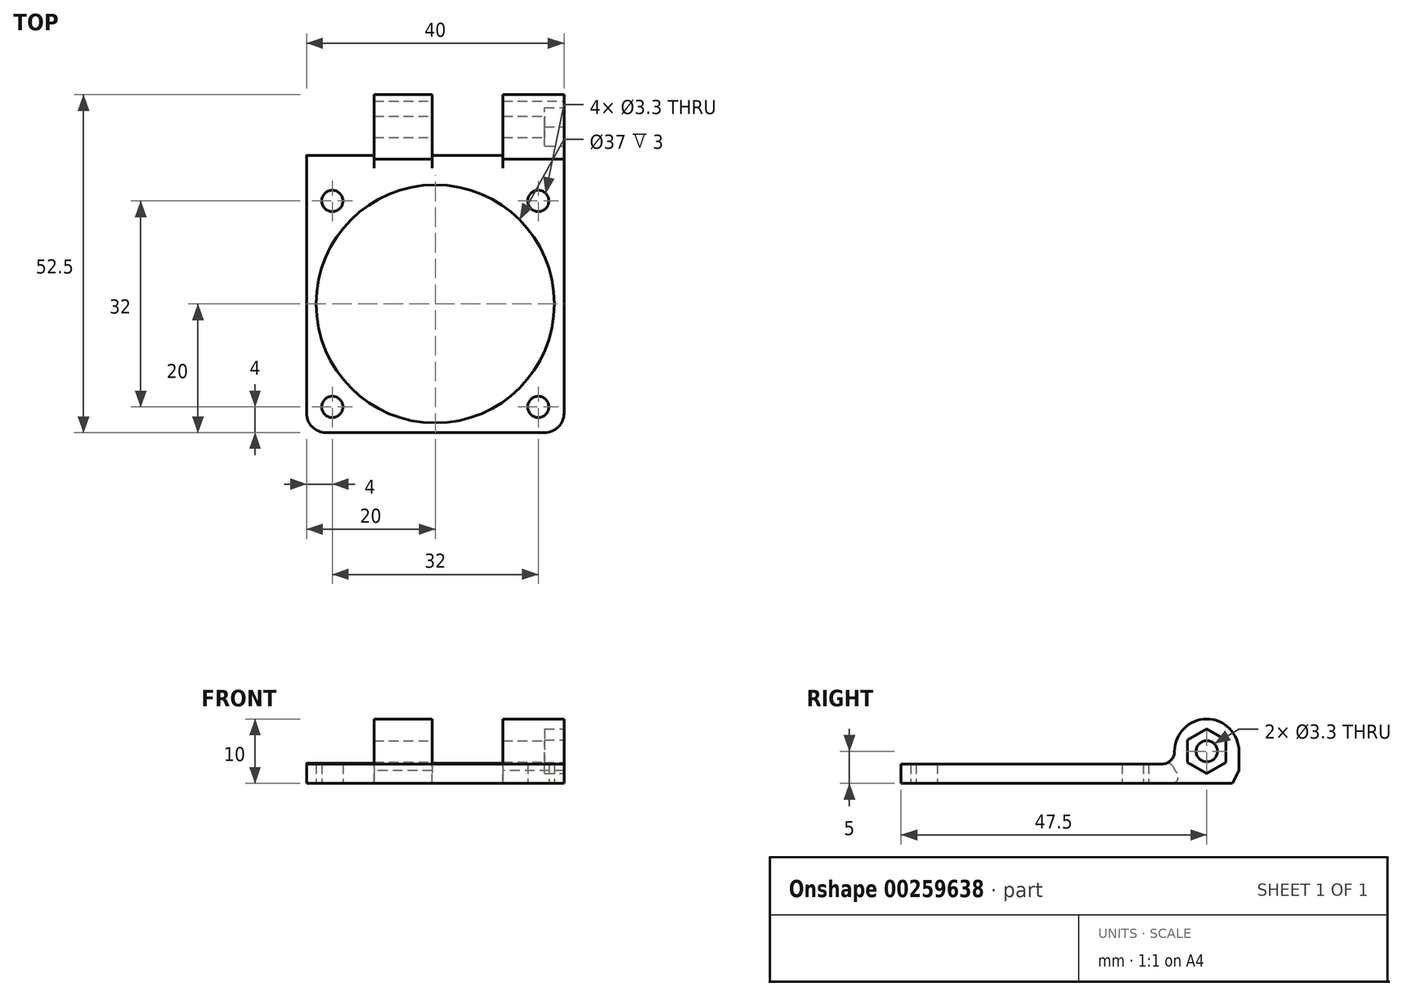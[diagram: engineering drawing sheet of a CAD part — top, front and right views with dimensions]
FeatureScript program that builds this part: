
annotation { "Feature Type Name" : "Feature", "Feature Type Description" : "" }
export const myFeature = defineFeature(function(context is Context, id is Id, definition is map)
    precondition{}
    {
        {
            var Q0;
            Q0=qCreatedBy(makeId("Top.planeOp"),FACE);
            var sketch = newSketch(context, id + "F0", { "sketchPlane" : qUnion([Q0])});
            skLineSegment(sketch, "E0.bottom", {"start": v(0, 0) * mm, "end": v(40, 0) * mm});
            skLineSegment(sketch, "E0.top", {"start": v(3, -45) * mm, "end": v(37, -45) * mm});
            skLineSegment(sketch, "E0.left", {"start": v(0, 0) * mm, "end": v(0, -42) * mm});
            skLineSegment(sketch, "E0.right", {"start": v(40, 0) * mm, "end": v(40, -42) * mm});
            skLineSegment(sketch, "E1", {"start": v(0, -5) * mm, "end": v(40, -5) * mm, "construction": true});
            skLineSegment(sketch, "E2", {"start": v(20, -5) * mm, "end": v(20, -45) * mm, "construction": true});
            skLineSegment(sketch, "E3", {"start": v(0, -5) * mm, "end": v(40, -45) * mm, "construction": true});
            skLineSegment(sketch, "E4", {"start": v(0, -45) * mm, "end": v(40, -5) * mm, "construction": true});
            skCircle(sketch, "E5", {"center": v(20, -25) * mm, "radius": 18.5 * mm});
            skCircle(sketch, "E6", {"center": v(4, -9) * mm, "radius": 1.65 * mm});
            skCircle(sketch, "E7", {"center": v(36, -9) * mm, "radius": 1.65 * mm});
            skCircle(sketch, "E8", {"center": v(36, -41) * mm, "radius": 1.65 * mm});
            skCircle(sketch, "E9", {"center": v(4, -41) * mm, "radius": 1.65 * mm});
            skPoint(sketch, "E10.visualSharp", {"position": v(0, -45) * mm});
            skArc(sketch, "E10.filletArc", {"start": v(0, -42) * mm, "mid": v(0.88, -44.12) * mm, "end": v(3, -45) * mm});
            skPoint(sketch, "E11.visualSharp", {"position": v(40, -45) * mm});
            skArc(sketch, "E11.filletArc", {"start": v(37, -45) * mm, "mid": v(39.12, -44.12) * mm, "end": v(40, -42) * mm});
            skSolve(sketch);
        }
        {
            var Q0;
            Q0 = qSketchRegion(id + "F0", true);
            extrude(context, id + "F1", {"entities" : qUnion([Q0]), "depth" : 3 * mm});
        }
        {
            var Q0;
            Q0=qCreatedBy(makeId("Right.planeOp"),FACE);
            var sketch = newSketch(context, id + "F2", { "sketchPlane" : qUnion([Q0])});
            skLineSegment(sketch, "E12.bottom", {"start": v(-2.5, 0) * mm, "end": v(7.5, 0) * mm});
            skLineSegment(sketch, "E12.left", {"start": v(-2.5, 0) * mm, "end": v(-2.5, 5) * mm});
            skArc(sketch, "E13", {"start": v(7.5, 5) * mm, "mid": v(2.5, 10) * mm, "end": v(-2.5, 5) * mm});
            skLineSegment(sketch, "E14", {"start": v(7.5, 5) * mm, "end": v(7.5, 0) * mm});
            skLineSegment(sketch, "E15", {"start": v(-2.5, 5) * mm, "end": v(7.5, 5) * mm, "construction": true});
            skLineSegment(sketch, "E16", {"start": v(2.5, 5) * mm, "end": v(2.5, 0) * mm, "construction": true});
            skSolve(sketch);
        }
        {
            var Q0;
            Q0 = qSketchRegion(id + "F2", true);
            extrude(context, id + "F3", {"entities" : qUnion([Q0]), "operationType" : NewBodyOperationType.ADD, "depth" : 40 * mm});
        }
        {
            var Q0;
            Q0=makeQuery(id+"F3.boolean.opBoolean","MERGE",FACE,{"derivedFrom":[makeQuery(id+"F1.opExtrude","SWEPT_FACE",FACE,{"disambiguationData":[OSD([sQuery(id+"F0.wireOp",EDGE,"E0.right")])]}),makeQuery(id+"F3.opExtrude","CAP_FACE",FACE,{"disambiguationData":[OSD([sQuery(id+"F2.wireOp",EDGE,"E12.bottom"),sQuery(id+"F2.wireOp",EDGE,"E12.left"),sQuery(id+"F2.wireOp",EDGE,"E13")])],"isStart":false})]});
            var sketch = newSketch(context, id + "F4", { "sketchPlane" : qUnion([Q0])});
            skLineSegment(sketch, "E17", {"start": v(0, 0) * mm, "end": v(2.5, 0) * mm, "construction": true});
            skLineSegment(sketch, "E18", {"start": v(2.5, 0) * mm, "end": v(2.5, 5) * mm, "construction": true});
            skCircle(sketch, "E19", {"center": v(2.5, 5) * mm, "radius": 1.65 * mm});
            skSolve(sketch);
        }
        {
            var Q0;
            Q0 = qSketchRegion(id + "F4", true);
            extrude(context, id + "F5", {"entities" : qUnion([Q0]), "operationType" : NewBodyOperationType.REMOVE, "endBound" : BoundingType.THROUGH_ALL, "oppositeDirection" : true, "depth" : 25 * mm});
        }
        {
            var Q0;
            Q0=makeQuery(id+"F3.boolean.opBoolean","MERGE",FACE,{"derivedFrom":[makeQuery(id+"F1.opExtrude","SWEPT_FACE",FACE,{"disambiguationData":[OSD([sQuery(id+"F0.wireOp",EDGE,"E0.right")])]}),makeQuery(id+"F3.opExtrude","CAP_FACE",FACE,{"disambiguationData":[OSD([sQuery(id+"F2.wireOp",EDGE,"E12.bottom"),sQuery(id+"F2.wireOp",EDGE,"E12.left"),sQuery(id+"F2.wireOp",EDGE,"E13")])],"isStart":false})]});
            var sketch = newSketch(context, id + "F6", { "sketchPlane" : qUnion([Q0])});
            skLineSegment(sketch, "E20", {"start": v(0, 0) * mm, "end": v(2.5, 0) * mm, "construction": true});
            skLineSegment(sketch, "E21", {"start": v(2.5, 0) * mm, "end": v(2.5, 5) * mm, "construction": true});
            skCircle(sketch, "E22.cCircle", {"center": v(2.5, 5) * mm, "radius": 3 * mm, "construction": true});
            skLineSegment(sketch, "E22.0", {"start": v(5.5, 6.73) * mm, "end": v(5.5, 3.27) * mm});
            skLineSegment(sketch, "E22.1", {"start": v(5.5, 3.27) * mm, "end": v(2.5, 1.54) * mm});
            skLineSegment(sketch, "E22.2", {"start": v(2.5, 1.54) * mm, "end": v(-0.5, 3.27) * mm});
            skLineSegment(sketch, "E22.3", {"start": v(-0.5, 3.27) * mm, "end": v(-0.5, 6.73) * mm});
            skLineSegment(sketch, "E22.4", {"start": v(-0.5, 6.73) * mm, "end": v(2.5, 8.46) * mm});
            skLineSegment(sketch, "E22.5", {"start": v(2.5, 8.46) * mm, "end": v(5.5, 6.73) * mm});
            skPoint(sketch, "E22.0.midPoint", {"position": v(5.5, 5) * mm});
            skSolve(sketch);
        }
        {
            var Q0;
            Q0 = qSketchRegion(id + "F6", true);
            extrude(context, id + "F7", {"entities" : qUnion([Q0]), "operationType" : NewBodyOperationType.REMOVE, "oppositeDirection" : true, "depth" : 3 * mm});
        }
        {
            var Q0;
            Q0=makeQuery(id+"F3.boolean.opBoolean","INTERSECT",EDGE,{"derivedFrom":[makeQuery(id+"F1.opExtrude","CAP_FACE",FACE,{"disambiguationData":[OSD([sQuery(id+"F0.wireOp",EDGE,"E0.bottom"),sQuery(id+"F0.wireOp",EDGE,"E0.top"),sQuery(id+"F0.wireOp",EDGE,"E0.left"),sQuery(id+"F0.wireOp",EDGE,"E0.right"),sQuery(id+"F0.wireOp",EDGE,"E5"),sQuery(id+"F0.wireOp",EDGE,"E6"),sQuery(id+"F0.wireOp",EDGE,"E7"),sQuery(id+"F0.wireOp",EDGE,"E8"),sQuery(id+"F0.wireOp",EDGE,"E9"),sQuery(id+"F0.wireOp",EDGE,"E10.filletArc"),sQuery(id+"F0.wireOp",EDGE,"E11.filletArc")])],"isStart":false}),makeQuery(id+"F3.opExtrude","SWEPT_FACE",FACE,{"disambiguationData":[OSD([sQuery(id+"F2.wireOp",EDGE,"E12.left")])]})]});
            fillet(context, id + "F8", {"entities" : qUnion([Q0]), "radius" : 2 * mm, "tangentPropagation" : true, "allowEdgeOverflow" : false});
        }
        {
            var Q0;
            Q0=makeQuery(id+"F3.boolean.opBoolean","MERGE",FACE,{"derivedFrom":[makeQuery(id+"F1.opExtrude","SWEPT_FACE",FACE,{"disambiguationData":[OSD([sQuery(id+"F0.wireOp",EDGE,"E0.right")])]}),makeQuery(id+"F3.opExtrude","CAP_FACE",FACE,{"disambiguationData":[OSD([sQuery(id+"F2.wireOp",EDGE,"E12.bottom"),sQuery(id+"F2.wireOp",EDGE,"E12.left"),sQuery(id+"F2.wireOp",EDGE,"E13")])],"isStart":false})]});
            cPlane(context, id + "F9", {"entities" : qUnion([Q0]), "cplaneType" : CPlaneType.OFFSET, "offset" : 9.5 * mm, "oppositeDirection" : true, "width" : 150 * mm, "height" : 150 * mm});
        }
        {
            var Q0;
            Q0=qCreatedBy(id+"F9.planeOp",FACE);
            var sketch = newSketch(context, id + "F10", { "sketchPlane" : qUnion([Q0])});
            skLineSegment(sketch, "E23", {"start": v(0, 0) * mm, "end": v(2.5, 0) * mm, "construction": true});
            skLineSegment(sketch, "E24", {"start": v(2.5, 0) * mm, "end": v(2.5, 5) * mm, "construction": true});
            skArc(sketch, "E25", {"start": v(8.25, 5) * mm, "mid": v(-1.57, 9.07) * mm, "end": v(2.5, -0.75) * mm});
            skLineSegment(sketch, "E26", {"start": v(2.5, -0.75) * mm, "end": v(8.25, -0.75) * mm});
            skLineSegment(sketch, "E27", {"start": v(8.25, -0.75) * mm, "end": v(8.25, 5) * mm});
            skSolve(sketch);
        }
        {
            var Q0;
            Q0 = qSketchRegion(id + "F10", true);
            extrude(context, id + "F11", {"entities" : qUnion([Q0]), "operationType" : NewBodyOperationType.REMOVE, "oppositeDirection" : true, "depth" : 11 * mm});
        }
        {
            var Q0;
            Q0=makeQuery(id+"F3.boolean.opBoolean","MERGE",FACE,{"derivedFrom":[makeQuery(id+"F1.opExtrude","SWEPT_FACE",FACE,{"disambiguationData":[OSD([sQuery(id+"F0.wireOp",EDGE,"E0.right")])]}),makeQuery(id+"F3.opExtrude","CAP_FACE",FACE,{"disambiguationData":[OSD([sQuery(id+"F2.wireOp",EDGE,"E12.bottom"),sQuery(id+"F2.wireOp",EDGE,"E12.left"),sQuery(id+"F2.wireOp",EDGE,"E13")])],"isStart":false})]});
            cPlane(context, id + "F12", {"entities" : qUnion([Q0]), "cplaneType" : CPlaneType.OFFSET, "offset" : 29.5 * mm, "oppositeDirection" : true, "width" : 150 * mm, "height" : 150 * mm});
        }
        {
            var Q0;
            Q0=qCreatedBy(id+"F12.planeOp",FACE);
            var sketch = newSketch(context, id + "F13", { "sketchPlane" : qUnion([Q0])});
            skLineSegment(sketch, "E28", {"start": v(0, 0) * mm, "end": v(2.5, 0) * mm, "construction": true});
            skLineSegment(sketch, "E29", {"start": v(2.5, 0) * mm, "end": v(2.5, 5) * mm, "construction": true});
            skArc(sketch, "E30", {"start": v(8.25, 5) * mm, "mid": v(-1.57, 9.07) * mm, "end": v(2.5, -0.75) * mm});
            skLineSegment(sketch, "E31", {"start": v(2.5, -0.75) * mm, "end": v(8.25, -0.75) * mm});
            skLineSegment(sketch, "E32", {"start": v(8.25, -0.75) * mm, "end": v(8.25, 5) * mm});
            skSolve(sketch);
        }
        {
            var Q0;
            Q0 = qSketchRegion(id + "F13", true);
            extrude(context, id + "F14", {"entities" : qUnion([Q0]), "operationType" : NewBodyOperationType.REMOVE, "endBound" : BoundingType.THROUGH_ALL, "oppositeDirection" : true, "depth" : 25 * mm});
        }
        {
            var Q0;
            {var subQ0=sQuery(id+"F0.wireOp",EDGE,"E0.right");var subQ1=sQuery(id+"F2.wireOp",EDGE,"E12.bottom");var subQ2=sQuery(id+"F2.wireOp",EDGE,"E14");Q0=makeQuery(id+"F11.boolean.opBoolean","SPLIT",EDGE,{"disambiguationData":[TD([makeQuery(id+"F1.opExtrude","SWEPT_FACE",FACE,{"disambiguationData":[OSD([subQ0])]})])],"derivedFrom":makeQuery(id+"F3.opExtrude","SWEPT_EDGE",EDGE,{"disambiguationData":[OSD([subQ1,subQ2])]})});}
            var Q1;
            {var subQ0=sQuery(id+"F0.wireOp",EDGE,"E0.left");var subQ1=sQuery(id+"F2.wireOp",EDGE,"E14");var subQ2=sQuery(id+"F2.wireOp",EDGE,"E12.bottom");Q1=makeQuery(id+"F11.boolean.opBoolean","SPLIT",EDGE,{"disambiguationData":[TD([makeQuery(id+"F1.opExtrude","SWEPT_FACE",FACE,{"disambiguationData":[OSD([subQ0])]})])],"derivedFrom":makeQuery(id+"F3.opExtrude","SWEPT_EDGE",EDGE,{"disambiguationData":[OSD([subQ2,subQ1])]})});}
            chamfer(context, id + "F15", {"entities" : qUnion([Q0, Q1]), "chamferType" : ChamferType.TWO_OFFSETS, "width1" : 2 * mm, "oppositeDirection" : false, "width2" : 1 * mm, "tangentPropagation" : true});
        }
        {
            var Q0;
            Q0=makeQuery(id+"F11.boolean.opBoolean","INTERSECT",EDGE,{"derivedFrom":[makeQuery(id+"F8.opFillet","BLEND_FACE",FACE,{"disambiguationData":[OSD([sQuery(id+"F0.wireOp",EDGE,"E0.bottom"),sQuery(id+"F0.wireOp",EDGE,"E0.top"),sQuery(id+"F0.wireOp",EDGE,"E0.left"),sQuery(id+"F0.wireOp",EDGE,"E0.right"),sQuery(id+"F0.wireOp",EDGE,"E5"),sQuery(id+"F0.wireOp",EDGE,"E6"),sQuery(id+"F0.wireOp",EDGE,"E7"),sQuery(id+"F0.wireOp",EDGE,"E8"),sQuery(id+"F0.wireOp",EDGE,"E9"),sQuery(id+"F0.wireOp",EDGE,"E10.filletArc"),sQuery(id+"F0.wireOp",EDGE,"E11.filletArc"),sQuery(id+"F2.wireOp",EDGE,"E12.left")])]}),makeQuery(id+"F11.opExtrude","SWEPT_FACE",FACE,{"disambiguationData":[OSD([sQuery(id+"F10.wireOp",EDGE,"E25")])]})]});
            var Q1;
            Q1=makeQuery(id+"F11.boolean.opBoolean","INTERSECT",EDGE,{"derivedFrom":[makeQuery(id+"F3.boolean.opBoolean","MERGE",FACE,{"derivedFrom":[makeQuery(id+"F1.opExtrude","CAP_FACE",FACE,{"disambiguationData":[OSD([sQuery(id+"F0.wireOp",EDGE,"E0.bottom"),sQuery(id+"F0.wireOp",EDGE,"E0.top"),sQuery(id+"F0.wireOp",EDGE,"E0.left"),sQuery(id+"F0.wireOp",EDGE,"E0.right"),sQuery(id+"F0.wireOp",EDGE,"E5"),sQuery(id+"F0.wireOp",EDGE,"E6"),sQuery(id+"F0.wireOp",EDGE,"E7"),sQuery(id+"F0.wireOp",EDGE,"E8"),sQuery(id+"F0.wireOp",EDGE,"E9"),sQuery(id+"F0.wireOp",EDGE,"E10.filletArc"),sQuery(id+"F0.wireOp",EDGE,"E11.filletArc")])],"isStart":true}),makeQuery(id+"F3.opExtrude","SWEPT_FACE",FACE,{"disambiguationData":[OSD([sQuery(id+"F2.wireOp",EDGE,"E12.bottom")])]})]}),makeQuery(id+"F11.opExtrude","SWEPT_FACE",FACE,{"disambiguationData":[OSD([sQuery(id+"F10.wireOp",EDGE,"E25")])]})]});
            var Q2;
            Q2=makeQuery(id+"F14.boolean.opBoolean","INTERSECT",EDGE,{"derivedFrom":[makeQuery(id+"F8.opFillet","BLEND_FACE",FACE,{"disambiguationData":[OSD([sQuery(id+"F0.wireOp",EDGE,"E0.bottom"),sQuery(id+"F0.wireOp",EDGE,"E0.top"),sQuery(id+"F0.wireOp",EDGE,"E0.left"),sQuery(id+"F0.wireOp",EDGE,"E0.right"),sQuery(id+"F0.wireOp",EDGE,"E5"),sQuery(id+"F0.wireOp",EDGE,"E6"),sQuery(id+"F0.wireOp",EDGE,"E7"),sQuery(id+"F0.wireOp",EDGE,"E8"),sQuery(id+"F0.wireOp",EDGE,"E9"),sQuery(id+"F0.wireOp",EDGE,"E10.filletArc"),sQuery(id+"F0.wireOp",EDGE,"E11.filletArc"),sQuery(id+"F2.wireOp",EDGE,"E12.left")])]}),makeQuery(id+"F14.opExtrude","SWEPT_FACE",FACE,{"disambiguationData":[OSD([sQuery(id+"F13.wireOp",EDGE,"E30")])]})]});
            var Q3;
            Q3=makeQuery(id+"F14.boolean.opBoolean","INTERSECT",EDGE,{"derivedFrom":[makeQuery(id+"F3.boolean.opBoolean","MERGE",FACE,{"derivedFrom":[makeQuery(id+"F1.opExtrude","CAP_FACE",FACE,{"disambiguationData":[OSD([sQuery(id+"F0.wireOp",EDGE,"E0.bottom"),sQuery(id+"F0.wireOp",EDGE,"E0.top"),sQuery(id+"F0.wireOp",EDGE,"E0.left"),sQuery(id+"F0.wireOp",EDGE,"E0.right"),sQuery(id+"F0.wireOp",EDGE,"E5"),sQuery(id+"F0.wireOp",EDGE,"E6"),sQuery(id+"F0.wireOp",EDGE,"E7"),sQuery(id+"F0.wireOp",EDGE,"E8"),sQuery(id+"F0.wireOp",EDGE,"E9"),sQuery(id+"F0.wireOp",EDGE,"E10.filletArc"),sQuery(id+"F0.wireOp",EDGE,"E11.filletArc")])],"isStart":true}),makeQuery(id+"F3.opExtrude","SWEPT_FACE",FACE,{"disambiguationData":[OSD([sQuery(id+"F2.wireOp",EDGE,"E12.bottom")])]})]}),makeQuery(id+"F14.opExtrude","SWEPT_FACE",FACE,{"disambiguationData":[OSD([sQuery(id+"F13.wireOp",EDGE,"E30")])]})]});
            fillet(context, id + "F16", {"entities" : qUnion([Q0, Q1, Q2, Q3]), "radius" : 1 * mm, "tangentPropagation" : true, "allowEdgeOverflow" : false});
        }
    });
